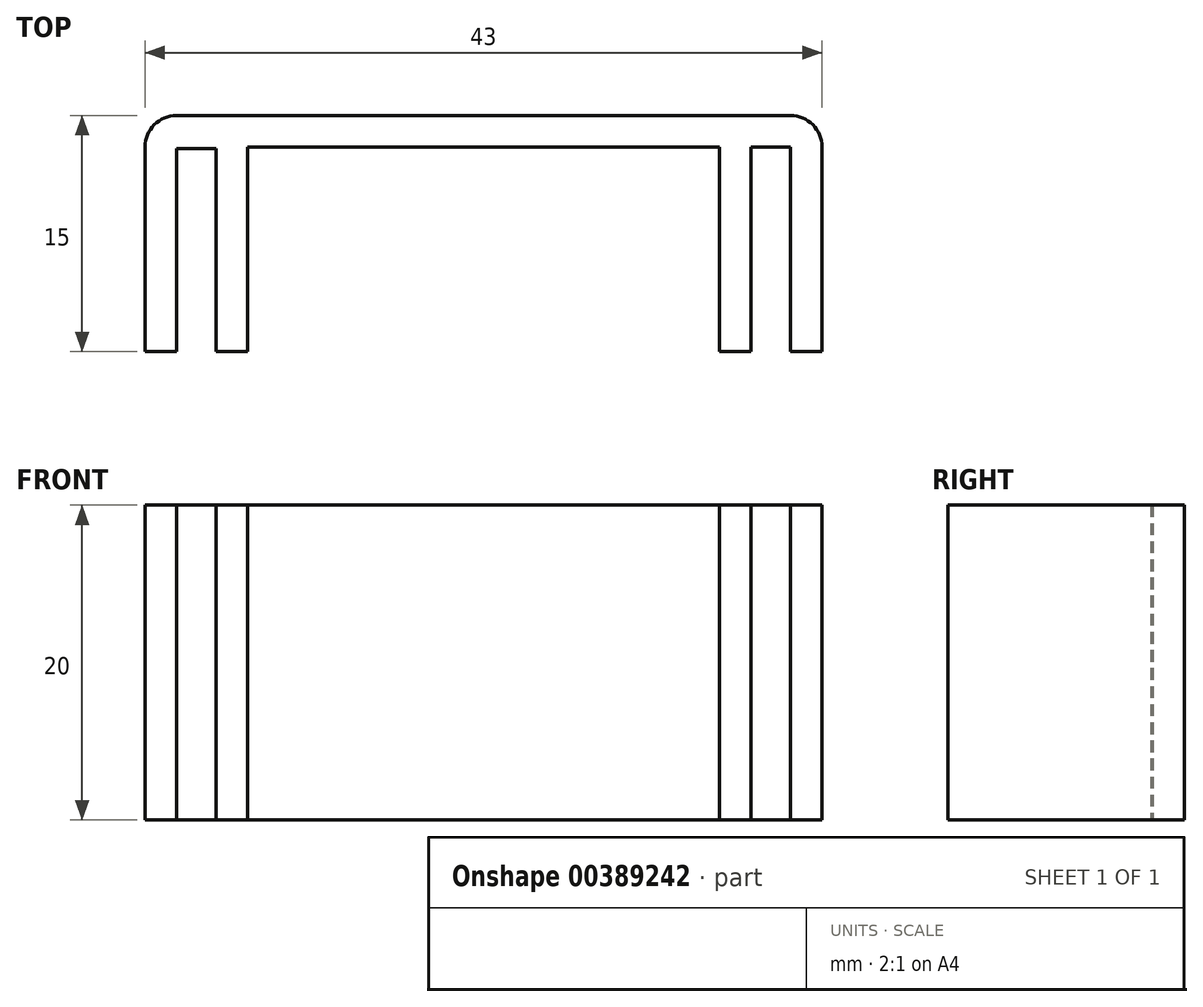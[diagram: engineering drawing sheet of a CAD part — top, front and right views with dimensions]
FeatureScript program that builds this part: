
annotation { "Feature Type Name" : "Feature", "Feature Type Description" : "" }
export const myFeature = defineFeature(function(context is Context, id is Id, definition is map)
    precondition{}
    {
        {
            var Q0;
            Q0=qCreatedBy(makeId("Top.planeOp"),FACE);
            var sketch = newSketch(context, id + "F0", { "sketchPlane" : qUnion([Q0])});
            skLineSegment(sketch, "E0.bottom", {"start": v(0, 0) * mm, "end": v(-2, 0) * mm});
            skLineSegment(sketch, "E0.top", {"start": v(0, 15) * mm, "end": v(-34, 15) * mm});
            skLineSegment(sketch, "E0.left", {"start": v(0, 0) * mm, "end": v(0, 13) * mm});
            skLineSegment(sketch, "E0.right", {"start": v(-34, 0) * mm, "end": v(-34, 12.9) * mm});
            skLineSegment(sketch, "E1", {"start": v(-36.5, 0) * mm, "end": v(-36.5, 12.9) * mm});
            skLineSegment(sketch, "E2", {"start": v(2.5, 13) * mm, "end": v(2.5, 0) * mm});
            skLineSegment(sketch, "E3.0", {"start": v(4.5, 15) * mm, "end": v(4.5, 0) * mm});
            skLineSegment(sketch, "E3.2", {"start": v(-38.5, 0) * mm, "end": v(-38.5, 15) * mm});
            skLineSegment(sketch, "E4", {"start": v(-36.5, 0) * mm, "end": v(-38.5, 0) * mm});
            skLineSegment(sketch, "E5", {"start": v(2.5, 0) * mm, "end": v(4.5, 0) * mm});
            skLineSegment(sketch, "E6.0", {"start": v(-2, 0) * mm, "end": v(-2, 13) * mm});
            skLineSegment(sketch, "E6.1", {"start": v(-2, 13) * mm, "end": v(-32, 13) * mm});
            skLineSegment(sketch, "E6.2", {"start": v(-32, 0) * mm, "end": v(-32, 13) * mm});
            skLineSegment(sketch, "E7", {"start": v(-27, 0) * mm, "end": v(-32, 0) * mm});
            skLineSegment(sketch, "E8", {"start": v(-34, 0) * mm, "end": v(-32, 0) * mm});
            skLineSegment(sketch, "E9", {"start": v(-2, 0) * mm, "end": v(0, 0) * mm});
            skLineSegment(sketch, "E10", {"start": v(-34, 12.9) * mm, "end": v(-36.5, 12.9) * mm});
            skLineSegment(sketch, "E11", {"start": v(-34, 15) * mm, "end": v(-36.5, 15) * mm});
            skLineSegment(sketch, "E12", {"start": v(0, 13) * mm, "end": v(2.5, 13) * mm});
            skLineSegment(sketch, "E13", {"start": v(0, 15) * mm, "end": v(2.5, 15) * mm});
            skLineSegment(sketch, "E14", {"start": v(2.5, 15) * mm, "end": v(4.5, 15) * mm});
            skLineSegment(sketch, "E15", {"start": v(-34, 15) * mm, "end": v(-38.5, 15) * mm});
            skLineSegment(sketch, "E16.trimOffspring", {"start": v(-27, 0) * mm, "end": v(-34, 0) * mm});
            skSolve(sketch);
        }
        {
            var Q0;
            Q0 = qSketchRegion(id + "F0", true);
            extrude(context, id + "F1", {"entities" : qUnion([Q0]), "depth" : 20 * mm, "offsetDistance" : 25 * mm});
        }
        {
            var Q0;
            Q0=makeQuery(id+"F1.opExtrude","SWEPT_EDGE",EDGE,{"disambiguationData":[OSD([sQuery(id+"F0.wireOp",EDGE,"E3.0"),sQuery(id+"F0.wireOp",EDGE,"E14")])]});
            var Q1;
            Q1=makeQuery(id+"F1.opExtrude","SWEPT_EDGE",EDGE,{"disambiguationData":[OSD([sQuery(id+"F0.wireOp",EDGE,"E3.2"),sQuery(id+"F0.wireOp",EDGE,"E15")])]});
            fillet(context, id + "F2", {"entities" : qUnion([Q0, Q1]), "radius" : 2 * mm, "tangentPropagation" : true, "allowEdgeOverflow" : false});
        }
    });
